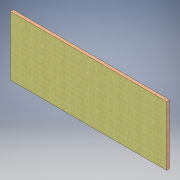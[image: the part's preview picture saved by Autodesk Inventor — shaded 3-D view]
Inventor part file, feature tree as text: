
AUTODESK INVENTOR PART (.ipt)
format: ipt  version: 2017 (Build 210142000, 142)  size: 119,808 bytes
history: native  units: in
note: dims shown in document units (in); Inventor stores cm internally (conversion verified against a paired STEP export)
features: extrude x1, sketch x1
ambient origin geometry x8: Origin, YZ Plane, XZ Plane, XY Plane, X Axis, Y Axis, Z Axis, Center Point
bodies: Solid1 (feature_tree)
feature tree (2):
  extrude  "Extrusion1"  Depth=31.4961in
  sketch  "Sketch1"  dims[d0=82.6772in d1=31.4961in d2=1.5748in d3=0.0in]
